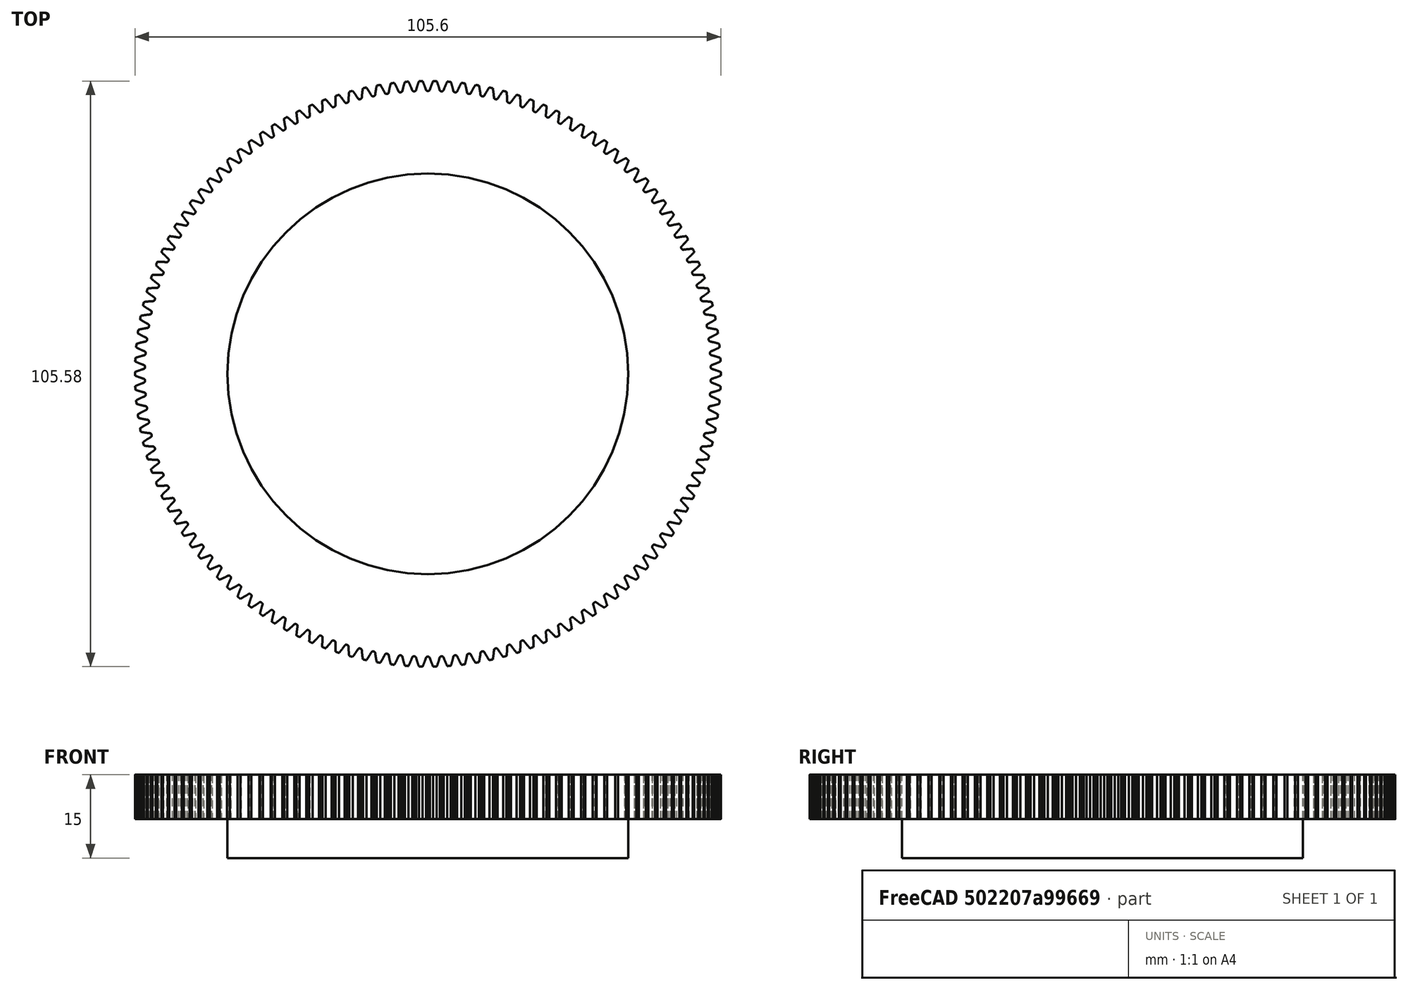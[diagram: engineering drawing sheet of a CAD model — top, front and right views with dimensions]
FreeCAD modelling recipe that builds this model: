
FCSTD DOCUMENT  (FreeCAD 0.15R4671 (Git))
Label: foton-37-140-ff
License: Creative Commons - Attribution - Share Alike license
LicenseURL: http://creativecommons.org/licenses/by-sa/3.0/
objects: Drawing::FeatureViewPart×3, Part::Part2DObjectPython×1, PartDesign::Pad×1, Sketcher::SketchObject×1, PartDesign::Pocket×1, Drawing::FeatureView×1, Drawing::FeaturePage×1
note: 6 computed .brp shape members not serialized (recipe doc carries the construction recipe); baked Part::Feature solids carry a one-line shape summary decoded from their .brp

FEATURE [Part::Part2DObjectPython] InvoluteGear  # Draft 2D object (typed FeaturePython)
  ExternalGear = true
  HighPrecision = true
  Modules = 0.8
  NumberOfTeeth = 130
  PressureAngle = 20
FEATURE [PartDesign::Pad] Pad001  label="Gear"
  Length = 8
  Length2 = 100
  Sketch = -> InvoluteGear
  Type = 0
FEATURE [Sketcher::SketchObject] Sketch
  Placement = pos=(0,0,8) rot=(0,0,1;0rad)
  Support = -> Pad001 [Face1042]
  sketch-geometry (1):
    g0: Circle CenterX=0 CenterY=0 CenterZ=0 NormalX=0 NormalY=0 NormalZ=1 Radius=36.125
  constraints (1):
    c: Radius(g0) = 36.125
FEATURE [PartDesign::Pocket] Pocket001  label="Focus Gear"
  Length = 15
  Sketch = -> Sketch
  Type = 0
FEATURE [Drawing::FeatureViewPart] topView
  Direction = (0,0,1)
  HiddenWidth = 0.15
  LineWidth = 0.35
  Rotation = 180
  ShowHiddenLines = true
  ShowSmoothLines = false
  Source = -> Pocket001
  Tolerance = 0.05
  ViewResult = <blob: 150118 chars omitted>
  Visible = true
  X = 100
  Y = 120
FEATURE [Drawing::FeatureViewPart] RightView
  Direction = (1,0,0)
  HiddenWidth = 0.15
  LineWidth = 0.35
  Rotation = 0
  ShowHiddenLines = true
  ShowSmoothLines = false
  Source = -> Pocket001
  Tolerance = 0.05
  ViewResult = <blob: 367258 chars omitted>
  Visible = true
  X = 215
  Y = 120
FEATURE [Drawing::FeatureViewPart] IsoView
  Direction = (1,1,1)
  HiddenWidth = 0.15
  LineWidth = 0.35
  Rotation = 60
  ShowHiddenLines = true
  ShowSmoothLines = false
  Source = -> Pocket001
  Tolerance = 0.05
  ViewResult = <blob: 254192 chars omitted>
  Visible = true
  X = 340
  Y = 125
FEATURE [Drawing::FeatureView] dim001
  Rotation = 0
  ViewResult = <g   >\n <circle cx ="100.000000" cy ="120.000000" r="0.500000" stroke="none" fill="rgb(0,0,0)" /> \n<line x1="65.201112" y1="107.851464" x2="100.000000" y2="120.000000" style="stroke:rgb(0,0,0);stroke-width:0.30" />\n<polygon points="65.893631,108.093227 68.396395,110.026146 69.670115,109.411624 69.055593,108.137904" style="fill:rgb(0,0,0);stroke:rgb(0,0,0);stroke-width:0" />\n<line x1="65.201112" y1="107.851464" x2="38.238246" y2="107.851464" style="stroke:rgb(0,0,0);stroke-width:0.30" />\n<text x="21.815410" y="108.831932" font-family="Arial" font-size="3.6" fill="rgb(0,0,0)" text-anchor="inherit"  >R36.125</text>\n<!--36.125-->\n<!--R%3.3f-->\n</g> 
  Visible = true
  X = 0
  Y = 0
FEATURE [Drawing::FeaturePage] AutoDrawing  label="Drawing"
  EditableTexts = FLOYD DIEBEL | 5/29/2015 | 1:1 | FOCUS GEAR | FOR LOMO FOTON 37-120MM
  Group = -> [topView,RightView,IsoView,dim001]
  Template = C:/Program Files/FreeCAD 0.15/data/Mod/Drawing/Templates/A3_Landscape.svg
